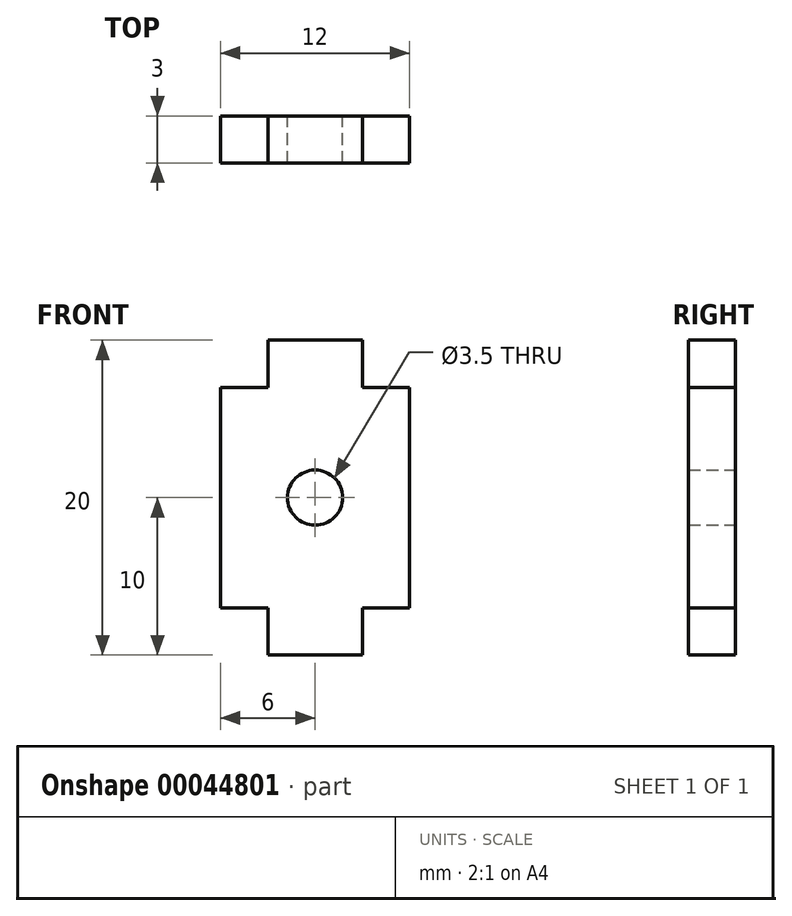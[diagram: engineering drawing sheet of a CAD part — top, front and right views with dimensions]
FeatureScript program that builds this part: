
annotation { "Feature Type Name" : "Feature", "Feature Type Description" : "" }
export const myFeature = defineFeature(function(context is Context, id is Id, definition is map)
    precondition{}
    {
        {
            var Q0;
            Q0=qCreatedBy(makeId("Front.planeOp"),FACE);
            var sketch = newSketch(context, id + "F0", { "sketchPlane" : qUnion([Q0])});
            skCircle(sketch, "E0", {"center": v(0, 0) * mm, "radius": 1.75 * mm});
            skLineSegment(sketch, "E1.rect.bottom", {"start": v(6, 7) * mm, "end": v(-6, 7) * mm});
            skLineSegment(sketch, "E1.rect.top", {"start": v(6, -7) * mm, "end": v(-6, -7) * mm});
            skLineSegment(sketch, "E1.rect.left", {"start": v(6, 7) * mm, "end": v(6, -7) * mm});
            skLineSegment(sketch, "E1.rect.right", {"start": v(-6, 7) * mm, "end": v(-6, -7) * mm});
            skLineSegment(sketch, "E2.bottom", {"start": v(-3, 7) * mm, "end": v(3, 7) * mm});
            skLineSegment(sketch, "E2.top", {"start": v(-3, 10) * mm, "end": v(3, 10) * mm});
            skLineSegment(sketch, "E2.left", {"start": v(-3, 7) * mm, "end": v(-3, 10) * mm});
            skLineSegment(sketch, "E2.right", {"start": v(3, 7) * mm, "end": v(3, 10) * mm});
            skPoint(sketch, "E3.oppositeSnap0", {"position": v(3, 8.5) * mm});
            skLineSegment(sketch, "E3.bottom", {"start": v(-3, -7) * mm, "end": v(3, -7) * mm});
            skLineSegment(sketch, "E3.top", {"start": v(-3, -10) * mm, "end": v(3, -10) * mm});
            skLineSegment(sketch, "E3.left", {"start": v(-3, -7) * mm, "end": v(-3, -10) * mm});
            skLineSegment(sketch, "E3.right", {"start": v(3, -7) * mm, "end": v(3, -10) * mm});
            skSolve(sketch);
        }
        {
            var Q0;
            Q0=qSketchRegion(id+"F0",true);
            extrude(context, id + "F1", {"entities" : qUnion([Q0]), "depth" : 3 * mm});
        }
    });
